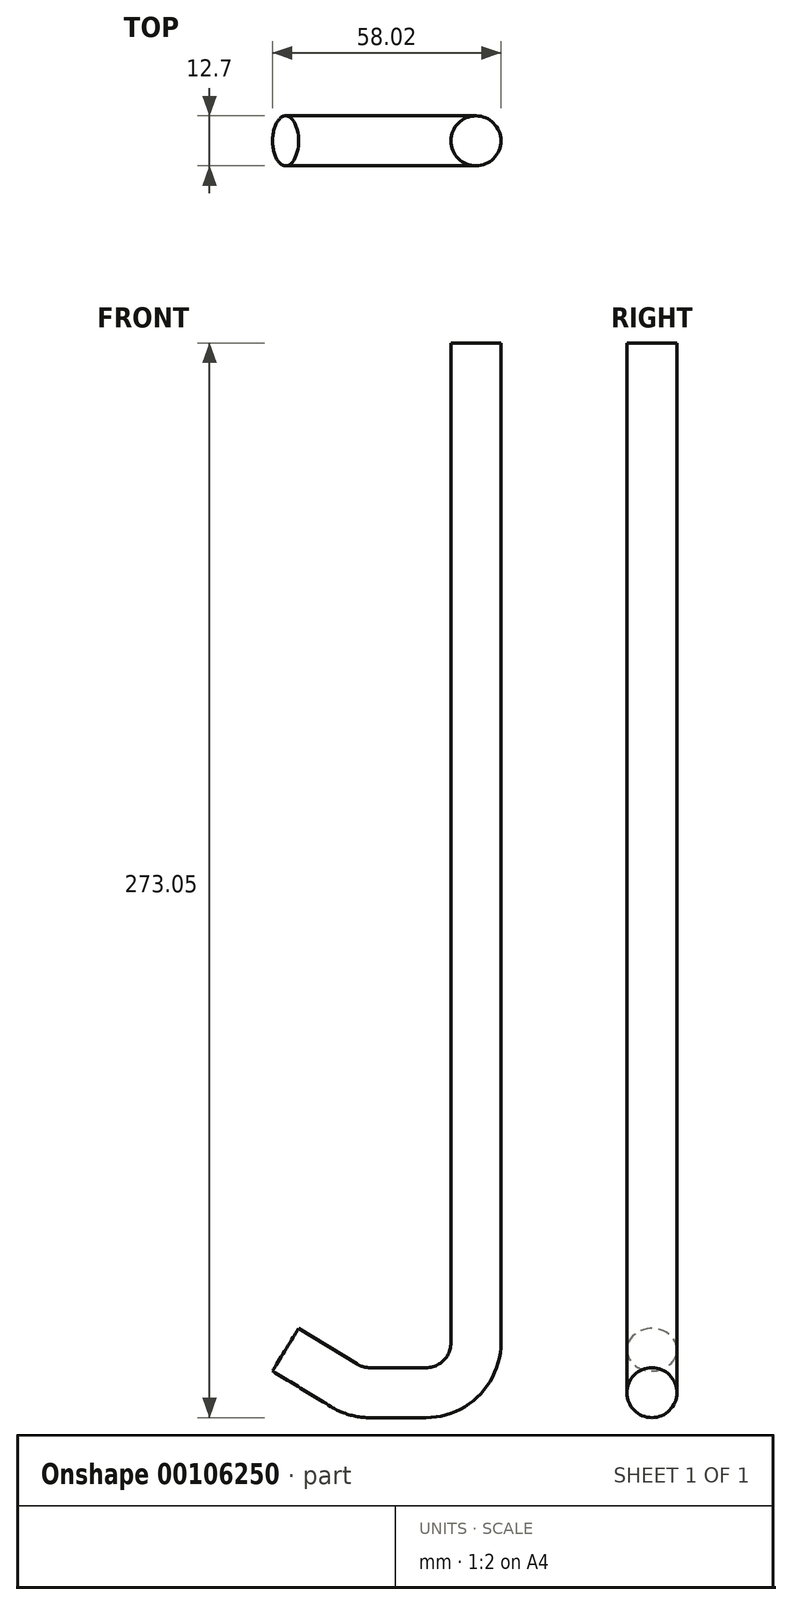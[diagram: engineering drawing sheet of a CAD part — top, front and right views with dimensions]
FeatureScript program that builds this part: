
annotation { "Feature Type Name" : "Feature", "Feature Type Description" : "" }
export const myFeature = defineFeature(function(context is Context, id is Id, definition is map)
    precondition{}
    {
        {
            var Q0;
            Q0=qCreatedBy(makeId("Front.planeOp"),FACE);
            var sketch = newSketch(context, id + "F0", { "sketchPlane" : qUnion([Q0])});
            skLineSegment(sketch, "E0", {"start": v(0, 200) * mm, "end": v(0, -54) * mm});
            skLineSegment(sketch, "E1", {"start": v(-12.7, -66.7) * mm, "end": v(-26.93, -66.7) * mm});
            skLineSegment(sketch, "E2", {"start": v(-33.55, -64.83) * mm, "end": v(-48.36, -55.78) * mm});
            skPoint(sketch, "E3.visualSharp", {"position": v(0, -66.7) * mm});
            skArc(sketch, "E3.filletArc", {"start": v(-12.7, -66.7) * mm, "mid": v(-3.72, -62.97) * mm, "end": v(0, -54) * mm});
            skPoint(sketch, "E4.visualSharp", {"position": v(-30.5, -66.7) * mm});
            skArc(sketch, "E4.filletArc", {"start": v(-33.55, -64.83) * mm, "mid": v(-30.37, -66.22) * mm, "end": v(-26.93, -66.7) * mm});
            skSolve(sketch);
        }
        {
            var Q0;
            Q0=sQuery(id+"F0.wireOp",VERTEX,"E0.start");
            var Q1;
            Q1=qCreatedBy(makeId("Top.planeOp"),FACE);
            cPlane(context, id + "F1", {"entities" : qUnion([Q0, Q1]), "cplaneType" : CPlaneType.PLANE_POINT, "offset" : 127 * mm, "width" : 152.4 * mm, "height" : 152.4 * mm});
        }
        {
            var Q0;
            Q0=qCreatedBy(id+"F1.planeOp",FACE);
            var sketch = newSketch(context, id + "F2", { "sketchPlane" : qUnion([Q0])});
            skCircle(sketch, "E5", {"center": v(0, 0) * mm, "radius": 6.35 * mm});
            skSolve(sketch);
        }
        {
            var Q0;
            Q0=makeQuery(id+"F2.imprint","IMPRINT",FACE,{"disambiguationData":[TD([[makeQuery(id+"F2.imprint","IMPRINT",EDGE,{"derivedFrom":sQuery(id+"F2.wireOp",EDGE,"E5")}),1.0]])]});
            var Q1;
            Q1=sQuery(id+"F0.wireOp",EDGE,"E0");
            var Q2;
            Q2=sQuery(id+"F0.wireOp",EDGE,"E3.filletArc");
            var Q3;
            Q3=sQuery(id+"F0.wireOp",EDGE,"E1");
            var Q4;
            Q4=sQuery(id+"F0.wireOp",EDGE,"E4.filletArc");
            var Q5;
            Q5=sQuery(id+"F0.wireOp",EDGE,"E2");
            sweep(context, id + "F3", {"profiles" : qUnion([Q0]), "path" : qUnion([Q1, Q2, Q3, Q4, Q5])});
        }
    });
